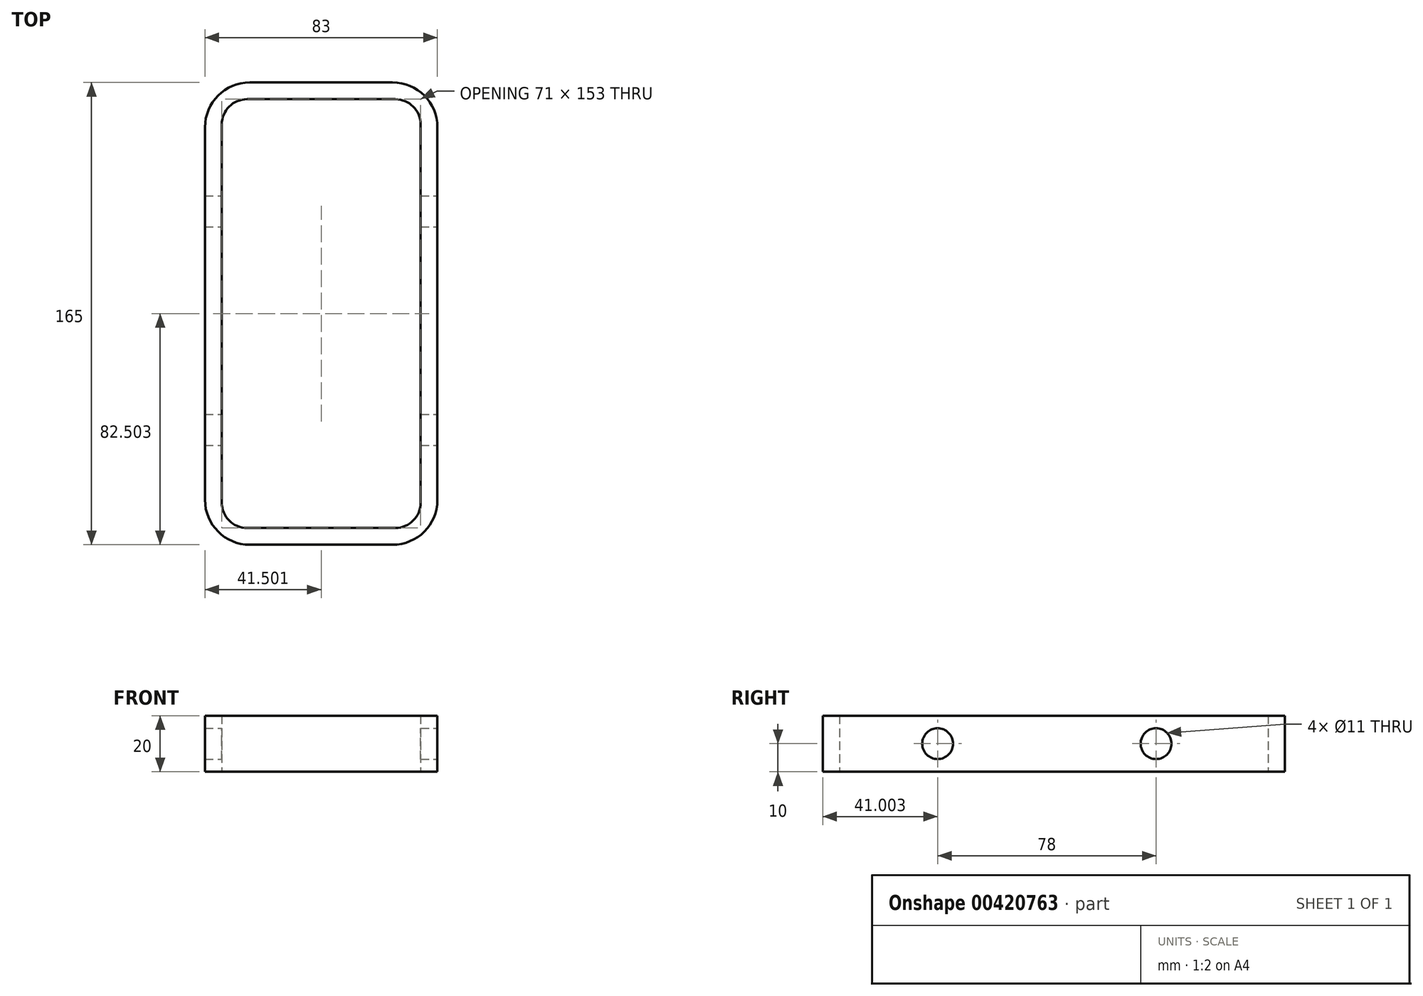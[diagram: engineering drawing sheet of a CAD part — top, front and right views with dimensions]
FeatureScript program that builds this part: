
annotation { "Feature Type Name" : "Feature", "Feature Type Description" : "" }
export const myFeature = defineFeature(function(context is Context, id is Id, definition is map)
    precondition{}
    {
        {
            var Q0;
            Q0=qCreatedBy(makeId("Top.planeOp"),FACE);
            var sketch = newSketch(context, id + "F0", { "sketchPlane" : qUnion([Q0])});
            skLineSegment(sketch, "E0.top", {"start": v(0, -35.14) * mm, "end": v(51, -35.14) * mm});
            skLineSegment(sketch, "E0.left", {"start": v(-16, 109.36) * mm, "end": v(-16, -19.14) * mm});
            skLineSegment(sketch, "E0.right", {"start": v(67, 109.36) * mm, "end": v(67, -19.14) * mm});
            skLineSegment(sketch, "E1.top", {"start": v(-1, -29.14) * mm, "end": v(52, -29.14) * mm});
            skLineSegment(sketch, "E1.left", {"start": v(-10, 106.15) * mm, "end": v(-10, -20.14) * mm});
            skLineSegment(sketch, "E1.right", {"start": v(61, 106.15) * mm, "end": v(61, -20.14) * mm});
            skPoint(sketch, "E2.visualSharp", {"position": v(-10, -29.14) * mm});
            skArc(sketch, "E2.filletArc", {"start": v(-10, -20.14) * mm, "mid": v(-7.37, -26.5) * mm, "end": v(-1, -29.14) * mm});
            skPoint(sketch, "E3.visualSharp", {"position": v(-16, -35.14) * mm});
            skArc(sketch, "E3.filletArc", {"start": v(-16, -19.14) * mm, "mid": v(-11.32, -30.45) * mm, "end": v(0, -35.14) * mm});
            skPoint(sketch, "E4.visualSharp", {"position": v(61, -29.14) * mm});
            skArc(sketch, "E4.filletArc", {"start": v(52, -29.14) * mm, "mid": v(58.35, -26.5) * mm, "end": v(61, -20.14) * mm});
            skPoint(sketch, "E5.visualSharp", {"position": v(67, -35.14) * mm});
            skArc(sketch, "E5.filletArc", {"start": v(51, -35.14) * mm, "mid": v(62.3, -30.45) * mm, "end": v(67, -19.14) * mm});
            skPoint(sketch, "E6", {"position": v(-16, 47.36) * mm});
            skPoint(sketch, "E7", {"position": v(67, 47.36) * mm});
            skLineSegment(sketch, "E8", {"start": v(-16, 47.36) * mm, "end": v(67, 47.36) * mm, "construction": true});
            skArc(sketch, "E9.MirrorCS", {"start": v(-16, 113.86) * mm, "mid": v(-11.32, 125.18) * mm, "end": v(0, 129.86) * mm});
            skArc(sketch, "E10.MirrorCS", {"start": v(-10, 114.86) * mm, "mid": v(-7.37, 121.23) * mm, "end": v(-1, 123.86) * mm});
            skLineSegment(sketch, "E11.MirrorCS", {"start": v(-1, 123.86) * mm, "end": v(52, 123.86) * mm});
            skLineSegment(sketch, "E12.MirrorCS", {"start": v(0, 129.86) * mm, "end": v(51, 129.86) * mm});
            skArc(sketch, "E13.MirrorCS", {"start": v(52, 123.86) * mm, "mid": v(58.35, 121.23) * mm, "end": v(61, 114.86) * mm});
            skArc(sketch, "E14.MirrorCS", {"start": v(51, 129.86) * mm, "mid": v(62.3, 125.18) * mm, "end": v(67, 113.86) * mm});
            skLineSegment(sketch, "E15", {"start": v(-10, 114.86) * mm, "end": v(-10, 106.15) * mm});
            skLineSegment(sketch, "E16", {"start": v(61, 114.86) * mm, "end": v(61, 106.15) * mm});
            skLineSegment(sketch, "E17", {"start": v(-16, 113.86) * mm, "end": v(-16, 109.36) * mm});
            skLineSegment(sketch, "E18", {"start": v(67, 113.86) * mm, "end": v(67, 109.36) * mm});
            skSolve(sketch);
        }
        {
            var Q0;
            Q0=makeQuery(id+"F0.imprint","IMPRINT",FACE,{"disambiguationData":[TD([[makeQuery(id+"F0.imprint","IMPRINT",EDGE,{"derivedFrom":sQuery(id+"F0.wireOp",EDGE,"E0.top")}),1.0]])]});
            var Q1;
            Q1=makeQuery(id+"F0.imprint","IMPRINT",FACE,{"disambiguationData":[TD([[makeQuery(id+"F0.imprint","IMPRINT",EDGE,{"derivedFrom":sQuery(id+"F0.wireOp",EDGE,"E9.MirrorCS")}),-1.0]])]});
            extrude(context, id + "F1", {"entities" : qUnion([Q0, Q1]), "depth" : 20 * mm});
        }
        {
            var Q0;
            Q0=makeQuery(id+"F1.opExtrude","SWEPT_FACE",FACE,{"disambiguationData":[OSD([sQuery(id+"F0.wireOp",EDGE,"E0.right")])]});
            cPlane(context, id + "F2", {"entities" : qUnion([Q0]), "cplaneType" : CPlaneType.OFFSET, "offset" : 25 * mm, "width" : 150 * mm, "height" : 150 * mm});
        }
        {
            var Q0;
            Q0=qCreatedBy(id+"F2.planeOp",FACE);
            var sketch = newSketch(context, id + "F3", { "sketchPlane" : qUnion([Q0])});
            skPoint(sketch, "E19", {"position": v(-8.48, 10) * mm});
            skPoint(sketch, "E20", {"position": v(113.89, 10) * mm});
            skLineSegment(sketch, "E21", {"start": v(-8.48, 10) * mm, "end": v(113.89, 10) * mm, "construction": true});
            skCircle(sketch, "E22", {"center": v(5.86, 10) * mm, "radius": 5.5 * mm});
            skCircle(sketch, "E23", {"center": v(83.86, 10) * mm, "radius": 5.5 * mm});
            skSolve(sketch);
        }
        {
            var Q0;
            Q0=makeQuery(id+"F3.imprint","IMPRINT",FACE,{"disambiguationData":[TD([[makeQuery(id+"F3.imprint","IMPRINT",EDGE,{"derivedFrom":sQuery(id+"F3.wireOp",EDGE,"E22")}),1.0]])]});
            var Q1;
            Q1=makeQuery(id+"F3.imprint","IMPRINT",FACE,{"disambiguationData":[TD([[makeQuery(id+"F3.imprint","IMPRINT",EDGE,{"derivedFrom":sQuery(id+"F3.wireOp",EDGE,"E23")}),1.0]])]});
            extrude(context, id + "F4", {"entities" : qUnion([Q0, Q1]), "operationType" : NewBodyOperationType.REMOVE, "oppositeDirection" : true, "depth" : 156 * mm});
        }
    });
